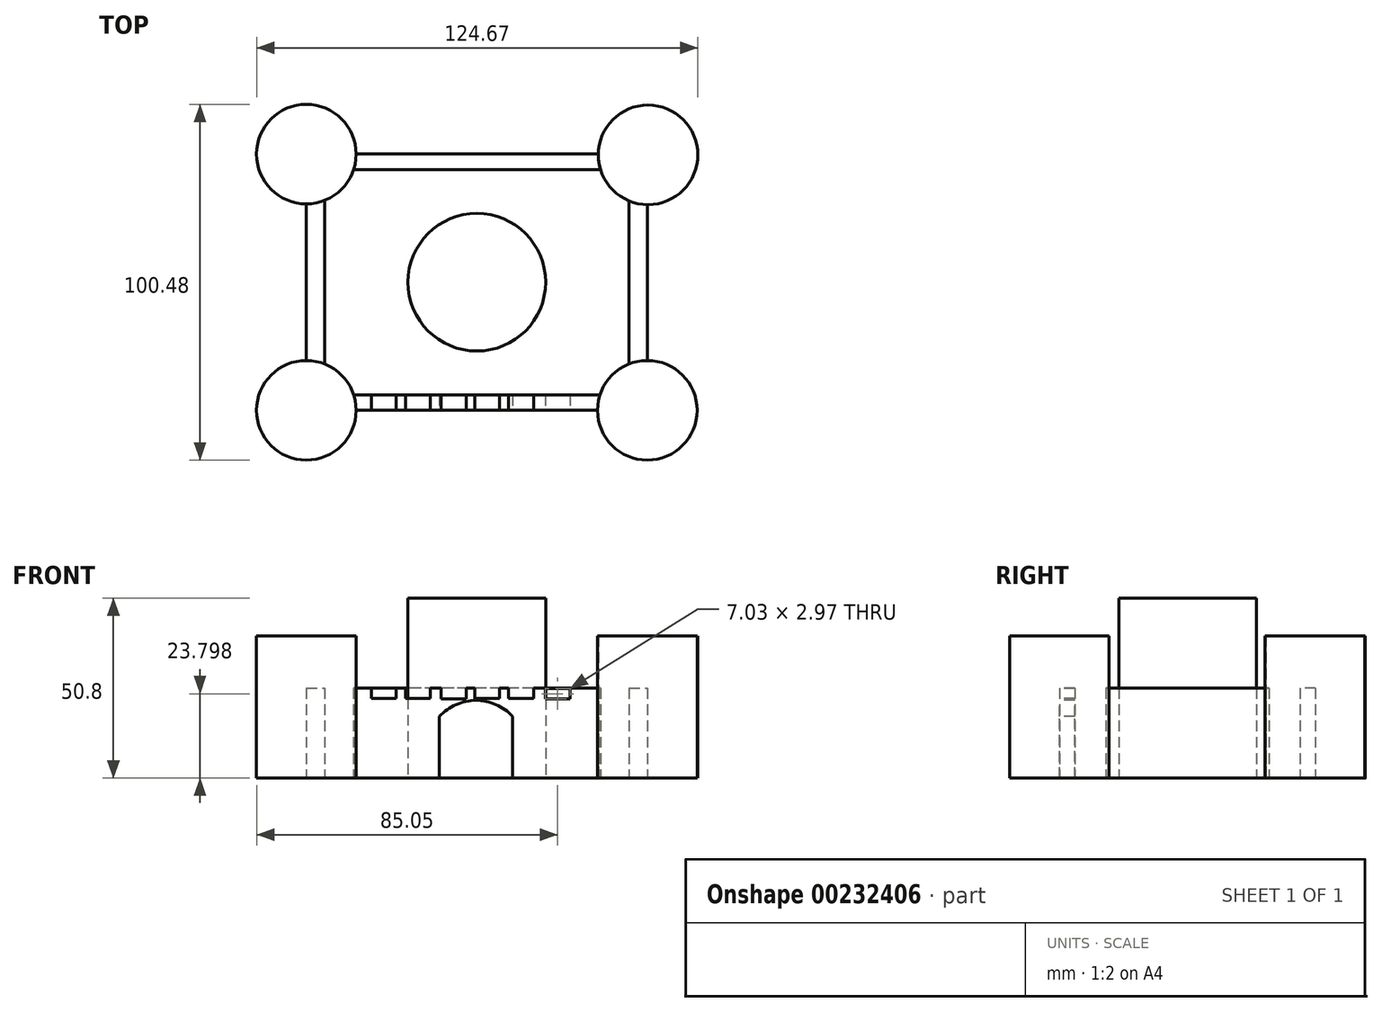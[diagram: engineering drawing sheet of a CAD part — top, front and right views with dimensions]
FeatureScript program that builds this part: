
annotation { "Feature Type Name" : "Feature", "Feature Type Description" : "" }
export const myFeature = defineFeature(function(context is Context, id is Id, definition is map)
    precondition{}
    {
        {
            var Q0;
            Q0=qCreatedBy(makeId("Top.planeOp"),FACE);
            var sketch = newSketch(context, id + "F0", { "sketchPlane" : qUnion([Q0])});
            skLineSegment(sketch, "E0.bottom", {"start": v(34.32, 36.18) * mm, "end": v(-34.11, 36.18) * mm});
            skLineSegment(sketch, "E0.top", {"start": v(34.11, -36.18) * mm, "end": v(-34.11, -36.18) * mm});
            skLineSegment(sketch, "E0.left", {"start": v(48.17, 21.91) * mm, "end": v(48.17, -22.12) * mm});
            skLineSegment(sketch, "E0.right", {"start": v(-48.17, 22.12) * mm, "end": v(-48.17, -22.12) * mm});
            skPoint(sketch, "E0.middle", {"position": v(0, 0) * mm});
            skCircle(sketch, "E1", {"center": v(0, 0) * mm, "radius": 19.44 * mm});
            skCircle(sketch, "E2", {"center": v(-48.17, 36.18) * mm, "radius": 14.06 * mm});
            skCircle(sketch, "E3", {"center": v(48.38, 35.97) * mm, "radius": 14.06 * mm});
            skCircle(sketch, "E4", {"center": v(-48.17, -36.18) * mm, "radius": 14.06 * mm});
            skCircle(sketch, "E5", {"center": v(48.17, -36.18) * mm, "radius": 14.06 * mm});
            skLineSegment(sketch, "E6.bottom", {"start": v(34.8, -31.84) * mm, "end": v(-34.8, -31.84) * mm});
            skLineSegment(sketch, "E6.top", {"start": v(34.94, 31.84) * mm, "end": v(-34.8, 31.84) * mm});
            skLineSegment(sketch, "E6.left", {"start": v(43, -23.1) * mm, "end": v(43, 22.98) * mm});
            skLineSegment(sketch, "E6.right", {"start": v(-43, -23.1) * mm, "end": v(-43, 23.1) * mm});
            skPoint(sketch, "E7.orphan", {"position": v(48.17, 36.18) * mm});
            skPoint(sketch, "E8.orphan", {"position": v(43, 31.84) * mm});
            skPoint(sketch, "E9.orphan", {"position": v(-43, 31.84) * mm});
            skLineSegment(sketch, "E10.trimOffspring", {"start": v(48.17, -36.18) * mm, "end": v(48.17, -36.18) * mm});
            skPoint(sketch, "E11.orphan", {"position": v(43, -31.84) * mm});
            skPoint(sketch, "E12.orphan", {"position": v(-43, -31.84) * mm});
            skSolve(sketch);
        }
        {
            var Q0;
            {var subQ0=sQuery(id+"F0.wireOp",EDGE,"E0.right");Q0=makeQuery(id+"F0.imprint","IMPRINT",FACE,{"disambiguationData":[TD([[makeQuery(id+"F0.imprint","IMPRINT",EDGE,{"derivedFrom":subQ0}),1.0]])]});}
            var Q1;
            {var subQ0=sQuery(id+"F0.wireOp",EDGE,"E0.top");Q1=makeQuery(id+"F0.imprint","IMPRINT",FACE,{"disambiguationData":[TD([[makeQuery(id+"F0.imprint","IMPRINT",EDGE,{"derivedFrom":subQ0}),-1.0]])]});}
            var Q2;
            {var subQ0=sQuery(id+"F0.wireOp",EDGE,"E0.left");Q2=makeQuery(id+"F0.imprint","IMPRINT",FACE,{"disambiguationData":[TD([[makeQuery(id+"F0.imprint","IMPRINT",EDGE,{"derivedFrom":subQ0}),-1.0]])]});}
            var Q3;
            {var subQ0=sQuery(id+"F0.wireOp",EDGE,"E0.bottom");Q3=makeQuery(id+"F0.imprint","IMPRINT",FACE,{"disambiguationData":[TD([[makeQuery(id+"F0.imprint","IMPRINT",EDGE,{"derivedFrom":subQ0}),1.0]])]});}
            extrude(context, id + "F1", {"entities" : qUnion([Q0, Q1, Q2, Q3]), "depth" : 25.4 * mm});
        }
        {
            var Q0;
            {var subQ0=sQuery(id+"F0.wireOp",EDGE,"E2");var subQ1=makeQuery(id+"F0.imprint","INTERSECT",VERTEX,{"derivedFrom":[sQuery(id+"F0.wireOp",EDGE,"E0.bottom"),subQ0]});Q0=makeQuery(id+"F0.imprint","IMPRINT",FACE,{"disambiguationData":[TD([[makeQuery(id+"F0.imprint","IMPRINT",EDGE,{"disambiguationData":[TD([[subQ1,-1.0]])],"derivedFrom":subQ0}),1.0]])]});}
            var Q1;
            {var subQ0=sQuery(id+"F0.wireOp",EDGE,"E3");var subQ1=makeQuery(id+"F0.imprint","INTERSECT",VERTEX,{"derivedFrom":[sQuery(id+"F0.wireOp",EDGE,"E0.bottom"),subQ0]});Q1=makeQuery(id+"F0.imprint","IMPRINT",FACE,{"disambiguationData":[TD([[makeQuery(id+"F0.imprint","IMPRINT",EDGE,{"disambiguationData":[TD([[subQ1,-1.0]])],"derivedFrom":subQ0}),1.0]])]});}
            var Q2;
            {var subQ0=sQuery(id+"F0.wireOp",EDGE,"E5");var subQ1=makeQuery(id+"F0.imprint","INTERSECT",VERTEX,{"derivedFrom":[sQuery(id+"F0.wireOp",EDGE,"E0.left"),subQ0]});Q2=makeQuery(id+"F0.imprint","IMPRINT",FACE,{"disambiguationData":[TD([[makeQuery(id+"F0.imprint","IMPRINT",EDGE,{"disambiguationData":[TD([[subQ1,-1.0]])],"derivedFrom":subQ0}),1.0]])]});}
            var Q3;
            {var subQ0=sQuery(id+"F0.wireOp",EDGE,"E4");var subQ1=makeQuery(id+"F0.imprint","INTERSECT",VERTEX,{"derivedFrom":[sQuery(id+"F0.wireOp",EDGE,"E0.top"),subQ0]});Q3=makeQuery(id+"F0.imprint","IMPRINT",FACE,{"disambiguationData":[TD([[makeQuery(id+"F0.imprint","IMPRINT",EDGE,{"disambiguationData":[TD([[subQ1,-1.0]])],"derivedFrom":subQ0}),1.0]])]});}
            extrude(context, id + "F2", {"entities" : qUnion([Q0, Q1, Q2, Q3]), "depth" : 40.13 * mm});
        }
        {
            var Q0;
            Q0=makeQuery(id+"F0.imprint","IMPRINT",FACE,{"disambiguationData":[TD([[makeQuery(id+"F0.imprint","IMPRINT",EDGE,{"derivedFrom":sQuery(id+"F0.wireOp",EDGE,"E1")}),1.0]])]});
            extrude(context, id + "F3", {"entities" : qUnion([Q0]), "depth" : 50.8 * mm});
        }
        {
            var Q0;
            Q0=makeQuery(id+"F1.opExtrude","SWEPT_FACE",FACE,{"disambiguationData":[OSD([sQuery(id+"F0.wireOp",EDGE,"E0.top")])]});
            var sketch = newSketch(context, id + "F4", { "sketchPlane" : qUnion([Q0])});
            skLineSegment(sketch, "E13.bottom", {"start": v(-10.54, 0) * mm, "end": v(10.13, 0) * mm});
            skLineSegment(sketch, "E13.left", {"start": v(-10.54, 0) * mm, "end": v(-10.54, 17.37) * mm});
            skLineSegment(sketch, "E13.right", {"start": v(10.13, 0) * mm, "end": v(10.13, 17.37) * mm});
            skArc(sketch, "E14", {"start": v(10.13, 17.37) * mm, "mid": v(-0.2, 21.93) * mm, "end": v(-10.54, 17.37) * mm});
            skLineSegment(sketch, "E15.bottom", {"start": v(-29.77, 25.4) * mm, "end": v(-22.74, 25.4) * mm});
            skLineSegment(sketch, "E15.top", {"start": v(-29.77, 22.43) * mm, "end": v(-22.74, 22.43) * mm});
            skLineSegment(sketch, "E15.left", {"start": v(-29.77, 25.4) * mm, "end": v(-29.77, 22.43) * mm});
            skLineSegment(sketch, "E15.right", {"start": v(-22.74, 25.4) * mm, "end": v(-22.74, 22.43) * mm});
            skLineSegment(sketch, "E16.bottom", {"start": v(-20.16, 25.4) * mm, "end": v(-13.13, 25.4) * mm});
            skLineSegment(sketch, "E16.top", {"start": v(-20.16, 22.44) * mm, "end": v(-13.13, 22.44) * mm});
            skLineSegment(sketch, "E16.left", {"start": v(-20.16, 25.4) * mm, "end": v(-20.16, 22.44) * mm});
            skLineSegment(sketch, "E16.right", {"start": v(-13.13, 25.4) * mm, "end": v(-13.13, 22.44) * mm});
            skLineSegment(sketch, "E17.bottom", {"start": v(-10.07, 25.4) * mm, "end": v(-3.05, 25.4) * mm});
            skLineSegment(sketch, "E17.top", {"start": v(-10.07, 22.31) * mm, "end": v(-3.05, 22.31) * mm});
            skLineSegment(sketch, "E17.left", {"start": v(-10.07, 25.4) * mm, "end": v(-10.07, 22.31) * mm});
            skLineSegment(sketch, "E17.right", {"start": v(-3.05, 25.4) * mm, "end": v(-3.05, 22.31) * mm});
            skLineSegment(sketch, "E18.bottom", {"start": v(-0.6, 25.4) * mm, "end": v(6.42, 25.4) * mm});
            skLineSegment(sketch, "E18.top", {"start": v(-0.6, 22.44) * mm, "end": v(6.42, 22.44) * mm});
            skLineSegment(sketch, "E18.left", {"start": v(-0.6, 25.4) * mm, "end": v(-0.6, 22.44) * mm});
            skLineSegment(sketch, "E18.right", {"start": v(6.42, 25.4) * mm, "end": v(6.42, 22.44) * mm});
            skLineSegment(sketch, "E19.bottom", {"start": v(8.98, 25.4) * mm, "end": v(16, 25.4) * mm});
            skLineSegment(sketch, "E19.top", {"start": v(8.98, 22.44) * mm, "end": v(16, 22.44) * mm});
            skLineSegment(sketch, "E19.left", {"start": v(8.98, 25.4) * mm, "end": v(8.98, 22.44) * mm});
            skLineSegment(sketch, "E19.right", {"start": v(16, 25.4) * mm, "end": v(16, 22.44) * mm});
            skLineSegment(sketch, "E20.bottom", {"start": v(19.3, 25.28) * mm, "end": v(26.34, 25.28) * mm});
            skLineSegment(sketch, "E20.top", {"start": v(19.3, 22.31) * mm, "end": v(26.34, 22.31) * mm});
            skLineSegment(sketch, "E20.left", {"start": v(19.3, 25.28) * mm, "end": v(19.3, 22.31) * mm});
            skLineSegment(sketch, "E20.right", {"start": v(26.34, 25.28) * mm, "end": v(26.34, 22.31) * mm});
            skSolve(sketch);
        }
        {
            var Q0;
            Q0=makeQuery(id+"F4.imprint","IMPRINT",FACE,{"disambiguationData":[TD([[makeQuery(id+"F4.imprint","IMPRINT",EDGE,{"derivedFrom":sQuery(id+"F4.wireOp",EDGE,"E13.bottom")}),-1.0]])]});
            extrude(context, id + "F5", {"entities" : qUnion([Q0]), "operationType" : NewBodyOperationType.REMOVE, "oppositeDirection" : true, "depth" : 4.57 * mm});
        }
        {
            var Q0;
            Q0 = qSketchRegion(id + "F4", true);
            var Q1;
            Q1=makeQuery(id+"F4.imprint","IMPRINT",FACE,{"disambiguationData":[TD([[makeQuery(id+"F4.imprint","IMPRINT",EDGE,{"derivedFrom":sQuery(id+"F4.wireOp",EDGE,"E15.bottom")}),1.0]])]});
            var Q2;
            {var subQ0=sQuery(id+"F4.wireOp",EDGE,"E16.top");Q2=makeQuery(id+"F4.imprint","IMPRINT",FACE,{"disambiguationData":[TD([[makeQuery(id+"F4.imprint","IMPRINT",EDGE,{"derivedFrom":subQ0}),1.0]])]});}
            var Q3;
            {var subQ0=sQuery(id+"F4.wireOp",EDGE,"E17.top");Q3=makeQuery(id+"F4.imprint","IMPRINT",FACE,{"disambiguationData":[TD([[makeQuery(id+"F4.imprint","IMPRINT",EDGE,{"derivedFrom":subQ0}),1.0]])]});}
            var Q4;
            {var subQ0=sQuery(id+"F4.wireOp",EDGE,"E18.top");Q4=makeQuery(id+"F4.imprint","IMPRINT",FACE,{"disambiguationData":[TD([[makeQuery(id+"F4.imprint","IMPRINT",EDGE,{"derivedFrom":subQ0}),1.0]])]});}
            var Q5;
            {var subQ0=sQuery(id+"F4.wireOp",EDGE,"E19.top");Q5=makeQuery(id+"F4.imprint","IMPRINT",FACE,{"disambiguationData":[TD([[makeQuery(id+"F4.imprint","IMPRINT",EDGE,{"derivedFrom":subQ0}),1.0]])]});}
            var Q6;
            Q6=makeQuery(id+"F4.imprint","IMPRINT",FACE,{"disambiguationData":[TD([[makeQuery(id+"F4.imprint","IMPRINT",EDGE,{"derivedFrom":sQuery(id+"F4.wireOp",EDGE,"E20.bottom")}),-1.0]])]});
            extrude(context, id + "F6", {"entities" : qUnion([Q0, Q1, Q2, Q3, Q4, Q5, Q6]), "operationType" : NewBodyOperationType.REMOVE, "oppositeDirection" : true, "depth" : 4.83 * mm});
        }
    });
